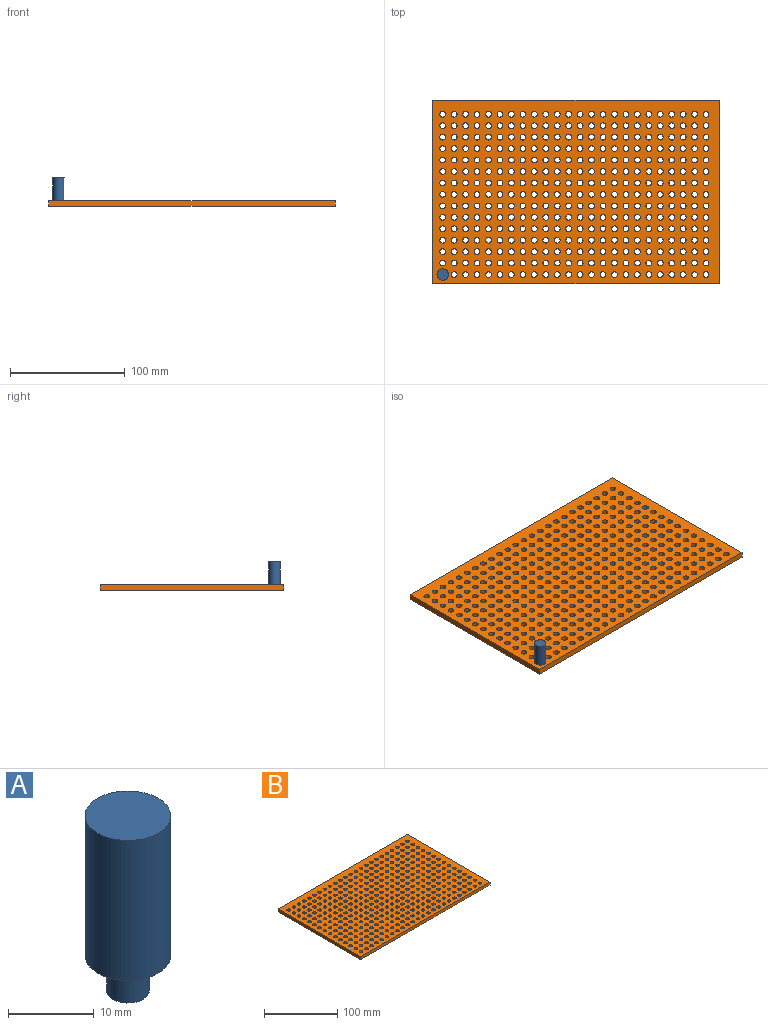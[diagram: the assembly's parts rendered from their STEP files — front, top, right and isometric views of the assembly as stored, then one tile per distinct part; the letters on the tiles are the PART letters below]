
ASSEMBLY  parts=2 mates=1
PART A: 5 faces, bbox 10x10x25 mm
  f0: plane 10x10mm, normal (0,0,-1), area 58.9mm2, adj f1,f4
  f1: cylinder r=2.5mm len=5mm, axis (0,0,-1), area 78.5mm2, adj f0,f2
  f2: plane 5x5mm, normal (0,0,-1), area 19.6mm2, adj f1
  f3: plane 10x10mm, normal (0,0,1), area 78.5mm2, adj f4
  f4: cylinder r=5mm len=20mm, axis (0,0,-1), area 628.3mm2, adj f0,f3
PART B: 366 faces, bbox 250x160x5 mm
  f0: plane 160x5mm, normal (1,0,0), area 800mm2, adj f1,f363,f364,f365
  f1: plane 250x5mm, normal (0,1,0), area 1250mm2, adj f0,f2,f364,f365
  f2: plane 160x5mm, normal (-1,0,0), area 800mm2, adj f1,f363,f364,f365
  f3: cylinder r=2.5mm len=5mm, axis (0,0,-1), area 78.5mm2, adj f364,f365
  f4: cylinder r=2.5mm len=5mm, axis (0,0,-1), area 78.5mm2, adj f364,f365
  f5: cylinder r=2.5mm len=5mm, axis (0,0,-1), area 78.5mm2, adj f364,f365
  f6: cylinder r=2.5mm len=5mm, axis (0,0,-1), area 78.5mm2, adj f364,f365
  f7: cylinder r=2.5mm len=5mm, axis (0,0,-1), area 78.5mm2, adj f364,f365
  f8: cylinder r=2.5mm len=5mm, axis (0,0,-1), area 78.5mm2, adj f364,f365
  f9: cylinder r=2.5mm len=5mm, axis (0,0,-1), area 78.5mm2, adj f364,f365
  f10: cylinder r=2.5mm len=5mm, axis (0,0,-1), area 78.5mm2, adj f364,f365
  f11: cylinder r=2.5mm len=5mm, axis (0,0,-1), area 78.5mm2, adj f364,f365
  f12: cylinder r=2.5mm len=5mm, axis (0,0,-1), area 78.5mm2, adj f364,f365
  f13: cylinder r=2.5mm len=5mm, axis (0,0,-1), area 78.5mm2, adj f364,f365
  f14: cylinder r=2.5mm len=5mm, axis (0,0,-1), area 78.5mm2, adj f364,f365
  f15: cylinder r=2.5mm len=5mm, axis (0,0,-1), area 78.5mm2, adj f364,f365
  f16: cylinder r=2.5mm len=5mm, axis (0,0,-1), area 78.5mm2, adj f364,f365
  f17: cylinder r=2.5mm len=5mm, axis (0,0,-1), area 78.5mm2, adj f364,f365
  f18: cylinder r=2.5mm len=5mm, axis (0,0,-1), area 78.5mm2, adj f364,f365
  f19: cylinder r=2.5mm len=5mm, axis (0,0,-1), area 78.5mm2, adj f364,f365
  f20: cylinder r=2.5mm len=5mm, axis (0,0,-1), area 78.5mm2, adj f364,f365
  f21: cylinder r=2.5mm len=5mm, axis (0,0,-1), area 78.5mm2, adj f364,f365
  f22: cylinder r=2.5mm len=5mm, axis (0,0,-1), area 78.5mm2, adj f364,f365
  f23: cylinder r=2.5mm len=5mm, axis (0,0,-1), area 78.5mm2, adj f364,f365
  f24: cylinder r=2.5mm len=5mm, axis (0,0,-1), area 78.5mm2, adj f364,f365
  f25: cylinder r=2.5mm len=5mm, axis (0,0,-1), area 78.5mm2, adj f364,f365
  f26: cylinder r=2.5mm len=5mm, axis (0,0,-1), area 78.5mm2, adj f364,f365
  f27: cylinder r=2.5mm len=5mm, axis (0,0,-1), area 78.5mm2, adj f364,f365
  f28: cylinder r=2.5mm len=5mm, axis (0,0,-1), area 78.5mm2, adj f364,f365
  f29: cylinder r=2.5mm len=5mm, axis (0,0,-1), area 78.5mm2, adj f364,f365
  f30: cylinder r=2.5mm len=5mm, axis (0,0,-1), area 78.5mm2, adj f364,f365
  f31: cylinder r=2.5mm len=5mm, axis (0,0,-1), area 78.5mm2, adj f364,f365
  f32: cylinder r=2.5mm len=5mm, axis (0,0,-1), area 78.5mm2, adj f364,f365
  f33: cylinder r=2.5mm len=5mm, axis (0,0,-1), area 78.5mm2, adj f364,f365
  f34: cylinder r=2.5mm len=5mm, axis (0,0,-1), area 78.5mm2, adj f364,f365
  f35: cylinder r=2.5mm len=5mm, axis (0,0,-1), area 78.5mm2, adj f364,f365
  f36: cylinder r=2.5mm len=5mm, axis (0,0,-1), area 78.5mm2, adj f364,f365
  f37: cylinder r=2.5mm len=5mm, axis (0,0,-1), area 78.5mm2, adj f364,f365
  f38: cylinder r=2.5mm len=5mm, axis (0,0,-1), area 78.5mm2, adj f364,f365
  f39: cylinder r=2.5mm len=5mm, axis (0,0,-1), area 78.5mm2, adj f364,f365
  f40: cylinder r=2.5mm len=5mm, axis (0,0,-1), area 78.5mm2, adj f364,f365
  f41: cylinder r=2.5mm len=5mm, axis (0,0,-1), area 78.5mm2, adj f364,f365
  f42: cylinder r=2.5mm len=5mm, axis (0,0,-1), area 78.5mm2, adj f364,f365
  f43: cylinder r=2.5mm len=5mm, axis (0,0,-1), area 78.5mm2, adj f364,f365
  f44: cylinder r=2.5mm len=5mm, axis (0,0,-1), area 78.5mm2, adj f364,f365
  f45: cylinder r=2.5mm len=5mm, axis (0,0,-1), area 78.5mm2, adj f364,f365
  f46: cylinder r=2.5mm len=5mm, axis (0,0,-1), area 78.5mm2, adj f364,f365
  f47: cylinder r=2.5mm len=5mm, axis (0,0,-1), area 78.5mm2, adj f364,f365
  f48: cylinder r=2.5mm len=5mm, axis (0,0,-1), area 78.5mm2, adj f364,f365
  f49: cylinder r=2.5mm len=5mm, axis (0,0,-1), area 78.5mm2, adj f364,f365
  f50: cylinder r=2.5mm len=5mm, axis (0,0,-1), area 78.5mm2, adj f364,f365
  f51: cylinder r=2.5mm len=5mm, axis (0,0,-1), area 78.5mm2, adj f364,f365
  f52: cylinder r=2.5mm len=5mm, axis (0,0,-1), area 78.5mm2, adj f364,f365
  f53: cylinder r=2.5mm len=5mm, axis (0,0,-1), area 78.5mm2, adj f364,f365
  f54: cylinder r=2.5mm len=5mm, axis (0,0,-1), area 78.5mm2, adj f364,f365
  f55: cylinder r=2.5mm len=5mm, axis (0,0,-1), area 78.5mm2, adj f364,f365
  f56: cylinder r=2.5mm len=5mm, axis (0,0,-1), area 78.5mm2, adj f364,f365
  f57: cylinder r=2.5mm len=5mm, axis (0,0,-1), area 78.5mm2, adj f364,f365
  f58: cylinder r=2.5mm len=5mm, axis (0,0,-1), area 78.5mm2, adj f364,f365
  f59: cylinder r=2.5mm len=5mm, axis (0,0,-1), area 78.5mm2, adj f364,f365
  f60: cylinder r=2.5mm len=5mm, axis (0,0,-1), area 78.5mm2, adj f364,f365
  f61: cylinder r=2.5mm len=5mm, axis (0,0,-1), area 78.5mm2, adj f364,f365
  f62: cylinder r=2.5mm len=5mm, axis (0,0,-1), area 78.5mm2, adj f364,f365
  f63: cylinder r=2.5mm len=5mm, axis (0,0,-1), area 78.5mm2, adj f364,f365
  f64: cylinder r=2.5mm len=5mm, axis (0,0,-1), area 78.5mm2, adj f364,f365
  f65: cylinder r=2.5mm len=5mm, axis (0,0,-1), area 78.5mm2, adj f364,f365
  f66: cylinder r=2.5mm len=5mm, axis (0,0,-1), area 78.5mm2, adj f364,f365
  f67: cylinder r=2.5mm len=5mm, axis (0,0,-1), area 78.5mm2, adj f364,f365
  f68: cylinder r=2.5mm len=5mm, axis (0,0,-1), area 78.5mm2, adj f364,f365
  f69: cylinder r=2.5mm len=5mm, axis (0,0,-1), area 78.5mm2, adj f364,f365
  f70: cylinder r=2.5mm len=5mm, axis (0,0,-1), area 78.5mm2, adj f364,f365
  f71: cylinder r=2.5mm len=5mm, axis (0,0,-1), area 78.5mm2, adj f364,f365
  f72: cylinder r=2.5mm len=5mm, axis (0,0,-1), area 78.5mm2, adj f364,f365
  f73: cylinder r=2.5mm len=5mm, axis (0,0,-1), area 78.5mm2, adj f364,f365
  f74: cylinder r=2.5mm len=5mm, axis (0,0,-1), area 78.5mm2, adj f364,f365
  f75: cylinder r=2.5mm len=5mm, axis (0,0,-1), area 78.5mm2, adj f364,f365
  f76: cylinder r=2.5mm len=5mm, axis (0,0,-1), area 78.5mm2, adj f364,f365
  f77: cylinder r=2.5mm len=5mm, axis (0,0,-1), area 78.5mm2, adj f364,f365
  f78: cylinder r=2.5mm len=5mm, axis (0,0,-1), area 78.5mm2, adj f364,f365
  f79: cylinder r=2.5mm len=5mm, axis (0,0,-1), area 78.5mm2, adj f364,f365
  f80: cylinder r=2.5mm len=5mm, axis (0,0,-1), area 78.5mm2, adj f364,f365
  f81: cylinder r=2.5mm len=5mm, axis (0,0,-1), area 78.5mm2, adj f364,f365
  f82: cylinder r=2.5mm len=5mm, axis (0,0,-1), area 78.5mm2, adj f364,f365
  f83: cylinder r=2.5mm len=5mm, axis (0,0,-1), area 78.5mm2, adj f364,f365
  f84: cylinder r=2.5mm len=5mm, axis (0,0,-1), area 78.5mm2, adj f364,f365
  f85: cylinder r=2.5mm len=5mm, axis (0,0,-1), area 78.5mm2, adj f364,f365
  f86: cylinder r=2.5mm len=5mm, axis (0,0,-1), area 78.5mm2, adj f364,f365
  f87: cylinder r=2.5mm len=5mm, axis (0,0,-1), area 78.5mm2, adj f364,f365
  f88: cylinder r=2.5mm len=5mm, axis (0,0,-1), area 78.5mm2, adj f364,f365
  f89: cylinder r=2.5mm len=5mm, axis (0,0,-1), area 78.5mm2, adj f364,f365
  f90: cylinder r=2.5mm len=5mm, axis (0,0,-1), area 78.5mm2, adj f364,f365
  f91: cylinder r=2.5mm len=5mm, axis (0,0,-1), area 78.5mm2, adj f364,f365
  f92: cylinder r=2.5mm len=5mm, axis (0,0,-1), area 78.5mm2, adj f364,f365
  f93: cylinder r=2.5mm len=5mm, axis (0,0,-1), area 78.5mm2, adj f364,f365
  f94: cylinder r=2.5mm len=5mm, axis (0,0,-1), area 78.5mm2, adj f364,f365
  f95: cylinder r=2.5mm len=5mm, axis (0,0,-1), area 78.5mm2, adj f364,f365
  f96: cylinder r=2.5mm len=5mm, axis (0,0,-1), area 78.5mm2, adj f364,f365
  f97: cylinder r=2.5mm len=5mm, axis (0,0,-1), area 78.5mm2, adj f364,f365
  f98: cylinder r=2.5mm len=5mm, axis (0,0,-1), area 78.5mm2, adj f364,f365
  f99: cylinder r=2.5mm len=5mm, axis (0,0,-1), area 78.5mm2, adj f364,f365
  f100: cylinder r=2.5mm len=5mm, axis (0,0,-1), area 78.5mm2, adj f364,f365
  f101: cylinder r=2.5mm len=5mm, axis (0,0,-1), area 78.5mm2, adj f364,f365
  f102: cylinder r=2.5mm len=5mm, axis (0,0,-1), area 78.5mm2, adj f364,f365
  f103: cylinder r=2.5mm len=5mm, axis (0,0,-1), area 78.5mm2, adj f364,f365
  f104: cylinder r=2.5mm len=5mm, axis (0,0,-1), area 78.5mm2, adj f364,f365
  f105: cylinder r=2.5mm len=5mm, axis (0,0,-1), area 78.5mm2, adj f364,f365
  f106: cylinder r=2.5mm len=5mm, axis (0,0,-1), area 78.5mm2, adj f364,f365
  f107: cylinder r=2.5mm len=5mm, axis (0,0,-1), area 78.5mm2, adj f364,f365
  f108: cylinder r=2.5mm len=5mm, axis (0,0,-1), area 78.5mm2, adj f364,f365
  f109: cylinder r=2.5mm len=5mm, axis (0,0,-1), area 78.5mm2, adj f364,f365
  f110: cylinder r=2.5mm len=5mm, axis (0,0,-1), area 78.5mm2, adj f364,f365
  f111: cylinder r=2.5mm len=5mm, axis (0,0,-1), area 78.5mm2, adj f364,f365
  f112: cylinder r=2.5mm len=5mm, axis (0,0,-1), area 78.5mm2, adj f364,f365
  f113: cylinder r=2.5mm len=5mm, axis (0,0,-1), area 78.5mm2, adj f364,f365
  f114: cylinder r=2.5mm len=5mm, axis (0,0,-1), area 78.5mm2, adj f364,f365
  f115: cylinder r=2.5mm len=5mm, axis (0,0,-1), area 78.5mm2, adj f364,f365
  f116: cylinder r=2.5mm len=5mm, axis (0,0,-1), area 78.5mm2, adj f364,f365
  f117: cylinder r=2.5mm len=5mm, axis (0,0,-1), area 78.5mm2, adj f364,f365
  f118: cylinder r=2.5mm len=5mm, axis (0,0,-1), area 78.5mm2, adj f364,f365
  f119: cylinder r=2.5mm len=5mm, axis (0,0,-1), area 78.5mm2, adj f364,f365
  f120: cylinder r=2.5mm len=5mm, axis (0,0,-1), area 78.5mm2, adj f364,f365
  f121: cylinder r=2.5mm len=5mm, axis (0,0,-1), area 78.5mm2, adj f364,f365
  f122: cylinder r=2.5mm len=5mm, axis (0,0,-1), area 78.5mm2, adj f364,f365
  f123: cylinder r=2.5mm len=5mm, axis (0,0,-1), area 78.5mm2, adj f364,f365
  f124: cylinder r=2.5mm len=5mm, axis (0,0,-1), area 78.5mm2, adj f364,f365
  f125: cylinder r=2.5mm len=5mm, axis (0,0,-1), area 78.5mm2, adj f364,f365
  f126: cylinder r=2.5mm len=5mm, axis (0,0,-1), area 78.5mm2, adj f364,f365
  f127: cylinder r=2.5mm len=5mm, axis (0,0,-1), area 78.5mm2, adj f364,f365
  f128: cylinder r=2.5mm len=5mm, axis (0,0,-1), area 78.5mm2, adj f364,f365
  f129: cylinder r=2.5mm len=5mm, axis (0,0,-1), area 78.5mm2, adj f364,f365
  f130: cylinder r=2.5mm len=5mm, axis (0,0,-1), area 78.5mm2, adj f364,f365
  f131: cylinder r=2.5mm len=5mm, axis (0,0,-1), area 78.5mm2, adj f364,f365
  f132: cylinder r=2.5mm len=5mm, axis (0,0,-1), area 78.5mm2, adj f364,f365
  f133: cylinder r=2.5mm len=5mm, axis (0,0,-1), area 78.5mm2, adj f364,f365
  f134: cylinder r=2.5mm len=5mm, axis (0,0,-1), area 78.5mm2, adj f364,f365
  f135: cylinder r=2.5mm len=5mm, axis (0,0,-1), area 78.5mm2, adj f364,f365
  f136: cylinder r=2.5mm len=5mm, axis (0,0,-1), area 78.5mm2, adj f364,f365
  f137: cylinder r=2.5mm len=5mm, axis (0,0,-1), area 78.5mm2, adj f364,f365
  f138: cylinder r=2.5mm len=5mm, axis (0,0,-1), area 78.5mm2, adj f364,f365
  f139: cylinder r=2.5mm len=5mm, axis (0,0,-1), area 78.5mm2, adj f364,f365
  f140: cylinder r=2.5mm len=5mm, axis (0,0,-1), area 78.5mm2, adj f364,f365
  f141: cylinder r=2.5mm len=5mm, axis (0,0,-1), area 78.5mm2, adj f364,f365
  f142: cylinder r=2.5mm len=5mm, axis (0,0,-1), area 78.5mm2, adj f364,f365
  f143: cylinder r=2.5mm len=5mm, axis (0,0,-1), area 78.5mm2, adj f364,f365
  f144: cylinder r=2.5mm len=5mm, axis (0,0,-1), area 78.5mm2, adj f364,f365
  f145: cylinder r=2.5mm len=5mm, axis (0,0,-1), area 78.5mm2, adj f364,f365
  f146: cylinder r=2.5mm len=5mm, axis (0,0,-1), area 78.5mm2, adj f364,f365
  f147: cylinder r=2.5mm len=5mm, axis (0,0,-1), area 78.5mm2, adj f364,f365
  f148: cylinder r=2.5mm len=5mm, axis (0,0,-1), area 78.5mm2, adj f364,f365
  f149: cylinder r=2.5mm len=5mm, axis (0,0,-1), area 78.5mm2, adj f364,f365
  f150: cylinder r=2.5mm len=5mm, axis (0,0,-1), area 78.5mm2, adj f364,f365
  f151: cylinder r=2.5mm len=5mm, axis (0,0,-1), area 78.5mm2, adj f364,f365
  f152: cylinder r=2.5mm len=5mm, axis (0,0,-1), area 78.5mm2, adj f364,f365
  f153: cylinder r=2.5mm len=5mm, axis (0,0,-1), area 78.5mm2, adj f364,f365
  f154: cylinder r=2.5mm len=5mm, axis (0,0,-1), area 78.5mm2, adj f364,f365
  f155: cylinder r=2.5mm len=5mm, axis (0,0,-1), area 78.5mm2, adj f364,f365
  f156: cylinder r=2.5mm len=5mm, axis (0,0,-1), area 78.5mm2, adj f364,f365
  f157: cylinder r=2.5mm len=5mm, axis (0,0,-1), area 78.5mm2, adj f364,f365
  f158: cylinder r=2.5mm len=5mm, axis (0,0,-1), area 78.5mm2, adj f364,f365
  f159: cylinder r=2.5mm len=5mm, axis (0,0,-1), area 78.5mm2, adj f364,f365
  f160: cylinder r=2.5mm len=5mm, axis (0,0,-1), area 78.5mm2, adj f364,f365
  f161: cylinder r=2.5mm len=5mm, axis (0,0,-1), area 78.5mm2, adj f364,f365
  f162: cylinder r=2.5mm len=5mm, axis (0,0,-1), area 78.5mm2, adj f364,f365
  f163: cylinder r=2.5mm len=5mm, axis (0,0,-1), area 78.5mm2, adj f364,f365
  f164: cylinder r=2.5mm len=5mm, axis (0,0,-1), area 78.5mm2, adj f364,f365
  f165: cylinder r=2.5mm len=5mm, axis (0,0,-1), area 78.5mm2, adj f364,f365
  f166: cylinder r=2.5mm len=5mm, axis (0,0,-1), area 78.5mm2, adj f364,f365
  f167: cylinder r=2.5mm len=5mm, axis (0,0,-1), area 78.5mm2, adj f364,f365
  f168: cylinder r=2.5mm len=5mm, axis (0,0,-1), area 78.5mm2, adj f364,f365
  f169: cylinder r=2.5mm len=5mm, axis (0,0,-1), area 78.5mm2, adj f364,f365
  f170: cylinder r=2.5mm len=5mm, axis (0,0,-1), area 78.5mm2, adj f364,f365
  f171: cylinder r=2.5mm len=5mm, axis (0,0,-1), area 78.5mm2, adj f364,f365
  f172: cylinder r=2.5mm len=5mm, axis (0,0,-1), area 78.5mm2, adj f364,f365
  f173: cylinder r=2.5mm len=5mm, axis (0,0,-1), area 78.5mm2, adj f364,f365
  f174: cylinder r=2.5mm len=5mm, axis (0,0,-1), area 78.5mm2, adj f364,f365
  f175: cylinder r=2.5mm len=5mm, axis (0,0,-1), area 78.5mm2, adj f364,f365
  f176: cylinder r=2.5mm len=5mm, axis (0,0,-1), area 78.5mm2, adj f364,f365
  f177: cylinder r=2.5mm len=5mm, axis (0,0,-1), area 78.5mm2, adj f364,f365
  f178: cylinder r=2.5mm len=5mm, axis (0,0,-1), area 78.5mm2, adj f364,f365
  f179: cylinder r=2.5mm len=5mm, axis (0,0,-1), area 78.5mm2, adj f364,f365
  f180: cylinder r=2.5mm len=5mm, axis (0,0,-1), area 78.5mm2, adj f364,f365
  f181: cylinder r=2.5mm len=5mm, axis (0,0,-1), area 78.5mm2, adj f364,f365
  f182: cylinder r=2.5mm len=5mm, axis (0,0,-1), area 78.5mm2, adj f364,f365
  f183: cylinder r=2.5mm len=5mm, axis (0,0,-1), area 78.5mm2, adj f364,f365
  f184: cylinder r=2.5mm len=5mm, axis (0,0,-1), area 78.5mm2, adj f364,f365
  f185: cylinder r=2.5mm len=5mm, axis (0,0,-1), area 78.5mm2, adj f364,f365
  f186: cylinder r=2.5mm len=5mm, axis (0,0,-1), area 78.5mm2, adj f364,f365
  f187: cylinder r=2.5mm len=5mm, axis (0,0,-1), area 78.5mm2, adj f364,f365
  f188: cylinder r=2.5mm len=5mm, axis (0,0,-1), area 78.5mm2, adj f364,f365
  f189: cylinder r=2.5mm len=5mm, axis (0,0,-1), area 78.5mm2, adj f364,f365
  f190: cylinder r=2.5mm len=5mm, axis (0,0,-1), area 78.5mm2, adj f364,f365
  f191: cylinder r=2.5mm len=5mm, axis (0,0,-1), area 78.5mm2, adj f364,f365
  f192: cylinder r=2.5mm len=5mm, axis (0,0,-1), area 78.5mm2, adj f364,f365
  f193: cylinder r=2.5mm len=5mm, axis (0,0,-1), area 78.5mm2, adj f364,f365
  f194: cylinder r=2.5mm len=5mm, axis (0,0,-1), area 78.5mm2, adj f364,f365
  f195: cylinder r=2.5mm len=5mm, axis (0,0,-1), area 78.5mm2, adj f364,f365
  f196: cylinder r=2.5mm len=5mm, axis (0,0,-1), area 78.5mm2, adj f364,f365
  f197: cylinder r=2.5mm len=5mm, axis (0,0,-1), area 78.5mm2, adj f364,f365
  f198: cylinder r=2.5mm len=5mm, axis (0,0,-1), area 78.5mm2, adj f364,f365
  f199: cylinder r=2.5mm len=5mm, axis (0,0,-1), area 78.5mm2, adj f364,f365
  f200: cylinder r=2.5mm len=5mm, axis (0,0,-1), area 78.5mm2, adj f364,f365
  f201: cylinder r=2.5mm len=5mm, axis (0,0,-1), area 78.5mm2, adj f364,f365
  f202: cylinder r=2.5mm len=5mm, axis (0,0,-1), area 78.5mm2, adj f364,f365
  f203: cylinder r=2.5mm len=5mm, axis (0,0,-1), area 78.5mm2, adj f364,f365
  f204: cylinder r=2.5mm len=5mm, axis (0,0,-1), area 78.5mm2, adj f364,f365
  f205: cylinder r=2.5mm len=5mm, axis (0,0,-1), area 78.5mm2, adj f364,f365
  f206: cylinder r=2.5mm len=5mm, axis (0,0,-1), area 78.5mm2, adj f364,f365
  f207: cylinder r=2.5mm len=5mm, axis (0,0,-1), area 78.5mm2, adj f364,f365
  f208: cylinder r=2.5mm len=5mm, axis (0,0,-1), area 78.5mm2, adj f364,f365
  f209: cylinder r=2.5mm len=5mm, axis (0,0,-1), area 78.5mm2, adj f364,f365
  f210: cylinder r=2.5mm len=5mm, axis (0,0,-1), area 78.5mm2, adj f364,f365
  f211: cylinder r=2.5mm len=5mm, axis (0,0,-1), area 78.5mm2, adj f364,f365
  f212: cylinder r=2.5mm len=5mm, axis (0,0,-1), area 78.5mm2, adj f364,f365
  f213: cylinder r=2.5mm len=5mm, axis (0,0,-1), area 78.5mm2, adj f364,f365
  f214: cylinder r=2.5mm len=5mm, axis (0,0,-1), area 78.5mm2, adj f364,f365
  f215: cylinder r=2.5mm len=5mm, axis (0,0,-1), area 78.5mm2, adj f364,f365
  f216: cylinder r=2.5mm len=5mm, axis (0,0,-1), area 78.5mm2, adj f364,f365
  f217: cylinder r=2.5mm len=5mm, axis (0,0,-1), area 78.5mm2, adj f364,f365
  f218: cylinder r=2.5mm len=5mm, axis (0,0,-1), area 78.5mm2, adj f364,f365
  f219: cylinder r=2.5mm len=5mm, axis (0,0,-1), area 78.5mm2, adj f364,f365
  f220: cylinder r=2.5mm len=5mm, axis (0,0,-1), area 78.5mm2, adj f364,f365
  f221: cylinder r=2.5mm len=5mm, axis (0,0,-1), area 78.5mm2, adj f364,f365
  f222: cylinder r=2.5mm len=5mm, axis (0,0,-1), area 78.5mm2, adj f364,f365
  f223: cylinder r=2.5mm len=5mm, axis (0,0,-1), area 78.5mm2, adj f364,f365
  f224: cylinder r=2.5mm len=5mm, axis (0,0,-1), area 78.5mm2, adj f364,f365
  f225: cylinder r=2.5mm len=5mm, axis (0,0,-1), area 78.5mm2, adj f364,f365
  f226: cylinder r=2.5mm len=5mm, axis (0,0,-1), area 78.5mm2, adj f364,f365
  f227: cylinder r=2.5mm len=5mm, axis (0,0,-1), area 78.5mm2, adj f364,f365
  f228: cylinder r=2.5mm len=5mm, axis (0,0,-1), area 78.5mm2, adj f364,f365
  f229: cylinder r=2.5mm len=5mm, axis (0,0,-1), area 78.5mm2, adj f364,f365
  f230: cylinder r=2.5mm len=5mm, axis (0,0,-1), area 78.5mm2, adj f364,f365
  f231: cylinder r=2.5mm len=5mm, axis (0,0,-1), area 78.5mm2, adj f364,f365
  f232: cylinder r=2.5mm len=5mm, axis (0,0,-1), area 78.5mm2, adj f364,f365
  f233: cylinder r=2.5mm len=5mm, axis (0,0,-1), area 78.5mm2, adj f364,f365
  f234: cylinder r=2.5mm len=5mm, axis (0,0,-1), area 78.5mm2, adj f364,f365
  f235: cylinder r=2.5mm len=5mm, axis (0,0,-1), area 78.5mm2, adj f364,f365
  f236: cylinder r=2.5mm len=5mm, axis (0,0,-1), area 78.5mm2, adj f364,f365
  f237: cylinder r=2.5mm len=5mm, axis (0,0,-1), area 78.5mm2, adj f364,f365
  f238: cylinder r=2.5mm len=5mm, axis (0,0,-1), area 78.5mm2, adj f364,f365
  f239: cylinder r=2.5mm len=5mm, axis (0,0,-1), area 78.5mm2, adj f364,f365
  f240: cylinder r=2.5mm len=5mm, axis (0,0,-1), area 78.5mm2, adj f364,f365
  f241: cylinder r=2.5mm len=5mm, axis (0,0,-1), area 78.5mm2, adj f364,f365
  f242: cylinder r=2.5mm len=5mm, axis (0,0,-1), area 78.5mm2, adj f364,f365
  f243: cylinder r=2.5mm len=5mm, axis (0,0,-1), area 78.5mm2, adj f364,f365
  f244: cylinder r=2.5mm len=5mm, axis (0,0,-1), area 78.5mm2, adj f364,f365
  f245: cylinder r=2.5mm len=5mm, axis (0,0,-1), area 78.5mm2, adj f364,f365
  f246: cylinder r=2.5mm len=5mm, axis (0,0,-1), area 78.5mm2, adj f364,f365
  f247: cylinder r=2.5mm len=5mm, axis (0,0,-1), area 78.5mm2, adj f364,f365
  f248: cylinder r=2.5mm len=5mm, axis (0,0,-1), area 78.5mm2, adj f364,f365
  f249: cylinder r=2.5mm len=5mm, axis (0,0,-1), area 78.5mm2, adj f364,f365
  f250: cylinder r=2.5mm len=5mm, axis (0,0,-1), area 78.5mm2, adj f364,f365
  f251: cylinder r=2.5mm len=5mm, axis (0,0,-1), area 78.5mm2, adj f364,f365
  f252: cylinder r=2.5mm len=5mm, axis (0,0,-1), area 78.5mm2, adj f364,f365
  f253: cylinder r=2.5mm len=5mm, axis (0,0,-1), area 78.5mm2, adj f364,f365
  f254: cylinder r=2.5mm len=5mm, axis (0,0,-1), area 78.5mm2, adj f364,f365
  f255: cylinder r=2.5mm len=5mm, axis (0,0,-1), area 78.5mm2, adj f364,f365
  f256: cylinder r=2.5mm len=5mm, axis (0,0,-1), area 78.5mm2, adj f364,f365
  f257: cylinder r=2.5mm len=5mm, axis (0,0,-1), area 78.5mm2, adj f364,f365
  f258: cylinder r=2.5mm len=5mm, axis (0,0,-1), area 78.5mm2, adj f364,f365
  f259: cylinder r=2.5mm len=5mm, axis (0,0,-1), area 78.5mm2, adj f364,f365
  f260: cylinder r=2.5mm len=5mm, axis (0,0,-1), area 78.5mm2, adj f364,f365
  f261: cylinder r=2.5mm len=5mm, axis (0,0,-1), area 78.5mm2, adj f364,f365
  f262: cylinder r=2.5mm len=5mm, axis (0,0,-1), area 78.5mm2, adj f364,f365
  f263: cylinder r=2.5mm len=5mm, axis (0,0,-1), area 78.5mm2, adj f364,f365
  f264: cylinder r=2.5mm len=5mm, axis (0,0,-1), area 78.5mm2, adj f364,f365
  f265: cylinder r=2.5mm len=5mm, axis (0,0,-1), area 78.5mm2, adj f364,f365
  f266: cylinder r=2.5mm len=5mm, axis (0,0,-1), area 78.5mm2, adj f364,f365
  f267: cylinder r=2.5mm len=5mm, axis (0,0,-1), area 78.5mm2, adj f364,f365
  f268: cylinder r=2.5mm len=5mm, axis (0,0,-1), area 78.5mm2, adj f364,f365
  f269: cylinder r=2.5mm len=5mm, axis (0,0,-1), area 78.5mm2, adj f364,f365
  f270: cylinder r=2.5mm len=5mm, axis (0,0,-1), area 78.5mm2, adj f364,f365
  f271: cylinder r=2.5mm len=5mm, axis (0,0,-1), area 78.5mm2, adj f364,f365
  f272: cylinder r=2.5mm len=5mm, axis (0,0,-1), area 78.5mm2, adj f364,f365
  f273: cylinder r=2.5mm len=5mm, axis (0,0,-1), area 78.5mm2, adj f364,f365
  f274: cylinder r=2.5mm len=5mm, axis (0,0,-1), area 78.5mm2, adj f364,f365
  f275: cylinder r=2.5mm len=5mm, axis (0,0,-1), area 78.5mm2, adj f364,f365
  f276: cylinder r=2.5mm len=5mm, axis (0,0,-1), area 78.5mm2, adj f364,f365
  f277: cylinder r=2.5mm len=5mm, axis (0,0,-1), area 78.5mm2, adj f364,f365
  f278: cylinder r=2.5mm len=5mm, axis (0,0,-1), area 78.5mm2, adj f364,f365
  f279: cylinder r=2.5mm len=5mm, axis (0,0,-1), area 78.5mm2, adj f364,f365
  f280: cylinder r=2.5mm len=5mm, axis (0,0,-1), area 78.5mm2, adj f364,f365
  f281: cylinder r=2.5mm len=5mm, axis (0,0,-1), area 78.5mm2, adj f364,f365
  f282: cylinder r=2.5mm len=5mm, axis (0,0,-1), area 78.5mm2, adj f364,f365
  f283: cylinder r=2.5mm len=5mm, axis (0,0,-1), area 78.5mm2, adj f364,f365
  f284: cylinder r=2.5mm len=5mm, axis (0,0,-1), area 78.5mm2, adj f364,f365
  f285: cylinder r=2.5mm len=5mm, axis (0,0,-1), area 78.5mm2, adj f364,f365
  f286: cylinder r=2.5mm len=5mm, axis (0,0,-1), area 78.5mm2, adj f364,f365
  f287: cylinder r=2.5mm len=5mm, axis (0,0,-1), area 78.5mm2, adj f364,f365
  f288: cylinder r=2.5mm len=5mm, axis (0,0,-1), area 78.5mm2, adj f364,f365
  f289: cylinder r=2.5mm len=5mm, axis (0,0,-1), area 78.5mm2, adj f364,f365
  f290: cylinder r=2.5mm len=5mm, axis (0,0,-1), area 78.5mm2, adj f364,f365
  f291: cylinder r=2.5mm len=5mm, axis (0,0,-1), area 78.5mm2, adj f364,f365
  f292: cylinder r=2.5mm len=5mm, axis (0,0,-1), area 78.5mm2, adj f364,f365
  f293: cylinder r=2.5mm len=5mm, axis (0,0,-1), area 78.5mm2, adj f364,f365
  f294: cylinder r=2.5mm len=5mm, axis (0,0,-1), area 78.5mm2, adj f364,f365
  f295: cylinder r=2.5mm len=5mm, axis (0,0,-1), area 78.5mm2, adj f364,f365
  f296: cylinder r=2.5mm len=5mm, axis (0,0,-1), area 78.5mm2, adj f364,f365
  f297: cylinder r=2.5mm len=5mm, axis (0,0,-1), area 78.5mm2, adj f364,f365
  f298: cylinder r=2.5mm len=5mm, axis (0,0,-1), area 78.5mm2, adj f364,f365
  f299: cylinder r=2.5mm len=5mm, axis (0,0,-1), area 78.5mm2, adj f364,f365
  f300: cylinder r=2.5mm len=5mm, axis (0,0,-1), area 78.5mm2, adj f364,f365
  f301: cylinder r=2.5mm len=5mm, axis (0,0,-1), area 78.5mm2, adj f364,f365
  f302: cylinder r=2.5mm len=5mm, axis (0,0,-1), area 78.5mm2, adj f364,f365
  f303: cylinder r=2.5mm len=5mm, axis (0,0,-1), area 78.5mm2, adj f364,f365
  f304: cylinder r=2.5mm len=5mm, axis (0,0,-1), area 78.5mm2, adj f364,f365
  f305: cylinder r=2.5mm len=5mm, axis (0,0,-1), area 78.5mm2, adj f364,f365
  f306: cylinder r=2.5mm len=5mm, axis (0,0,-1), area 78.5mm2, adj f364,f365
  f307: cylinder r=2.5mm len=5mm, axis (0,0,-1), area 78.5mm2, adj f364,f365
  f308: cylinder r=2.5mm len=5mm, axis (0,0,-1), area 78.5mm2, adj f364,f365
  f309: cylinder r=2.5mm len=5mm, axis (0,0,-1), area 78.5mm2, adj f364,f365
  f310: cylinder r=2.5mm len=5mm, axis (0,0,-1), area 78.5mm2, adj f364,f365
  f311: cylinder r=2.5mm len=5mm, axis (0,0,-1), area 78.5mm2, adj f364,f365
  f312: cylinder r=2.5mm len=5mm, axis (0,0,-1), area 78.5mm2, adj f364,f365
  f313: cylinder r=2.5mm len=5mm, axis (0,0,-1), area 78.5mm2, adj f364,f365
  f314: cylinder r=2.5mm len=5mm, axis (0,0,-1), area 78.5mm2, adj f364,f365
  f315: cylinder r=2.5mm len=5mm, axis (0,0,-1), area 78.5mm2, adj f364,f365
  f316: cylinder r=2.5mm len=5mm, axis (0,0,-1), area 78.5mm2, adj f364,f365
  f317: cylinder r=2.5mm len=5mm, axis (0,0,-1), area 78.5mm2, adj f364,f365
  f318: cylinder r=2.5mm len=5mm, axis (0,0,-1), area 78.5mm2, adj f364,f365
  f319: cylinder r=2.5mm len=5mm, axis (0,0,-1), area 78.5mm2, adj f364,f365
  f320: cylinder r=2.5mm len=5mm, axis (0,0,-1), area 78.5mm2, adj f364,f365
  f321: cylinder r=2.5mm len=5mm, axis (0,0,-1), area 78.5mm2, adj f364,f365
  f322: cylinder r=2.5mm len=5mm, axis (0,0,-1), area 78.5mm2, adj f364,f365
  f323: cylinder r=2.5mm len=5mm, axis (0,0,-1), area 78.5mm2, adj f364,f365
  f324: cylinder r=2.5mm len=5mm, axis (0,0,-1), area 78.5mm2, adj f364,f365
  f325: cylinder r=2.5mm len=5mm, axis (0,0,-1), area 78.5mm2, adj f364,f365
  f326: cylinder r=2.5mm len=5mm, axis (0,0,-1), area 78.5mm2, adj f364,f365
  f327: cylinder r=2.5mm len=5mm, axis (0,0,-1), area 78.5mm2, adj f364,f365
  f328: cylinder r=2.5mm len=5mm, axis (0,0,-1), area 78.5mm2, adj f364,f365
  f329: cylinder r=2.5mm len=5mm, axis (0,0,-1), area 78.5mm2, adj f364,f365
  f330: cylinder r=2.5mm len=5mm, axis (0,0,-1), area 78.5mm2, adj f364,f365
  f331: cylinder r=2.5mm len=5mm, axis (0,0,-1), area 78.5mm2, adj f364,f365
  f332: cylinder r=2.5mm len=5mm, axis (0,0,-1), area 78.5mm2, adj f364,f365
  f333: cylinder r=2.5mm len=5mm, axis (0,0,-1), area 78.5mm2, adj f364,f365
  f334: cylinder r=2.5mm len=5mm, axis (0,0,-1), area 78.5mm2, adj f364,f365
  f335: cylinder r=2.5mm len=5mm, axis (0,0,-1), area 78.5mm2, adj f364,f365
  f336: cylinder r=2.5mm len=5mm, axis (0,0,-1), area 78.5mm2, adj f364,f365
  f337: cylinder r=2.5mm len=5mm, axis (0,0,-1), area 78.5mm2, adj f364,f365
  f338: cylinder r=2.5mm len=5mm, axis (0,0,-1), area 78.5mm2, adj f364,f365
  f339: cylinder r=2.5mm len=5mm, axis (0,0,-1), area 78.5mm2, adj f364,f365
  f340: cylinder r=2.5mm len=5mm, axis (0,0,-1), area 78.5mm2, adj f364,f365
  f341: cylinder r=2.5mm len=5mm, axis (0,0,-1), area 78.5mm2, adj f364,f365
  f342: cylinder r=2.5mm len=5mm, axis (0,0,-1), area 78.5mm2, adj f364,f365
  f343: cylinder r=2.5mm len=5mm, axis (0,0,-1), area 78.5mm2, adj f364,f365
  f344: cylinder r=2.5mm len=5mm, axis (0,0,-1), area 78.5mm2, adj f364,f365
  f345: cylinder r=2.5mm len=5mm, axis (0,0,-1), area 78.5mm2, adj f364,f365
  f346: cylinder r=2.5mm len=5mm, axis (0,0,-1), area 78.5mm2, adj f364,f365
  f347: cylinder r=2.5mm len=5mm, axis (0,0,-1), area 78.5mm2, adj f364,f365
  f348: cylinder r=2.5mm len=5mm, axis (0,0,-1), area 78.5mm2, adj f364,f365
  f349: cylinder r=2.5mm len=5mm, axis (0,0,-1), area 78.5mm2, adj f364,f365
  f350: cylinder r=2.5mm len=5mm, axis (0,0,-1), area 78.5mm2, adj f364,f365
  f351: cylinder r=2.5mm len=5mm, axis (0,0,-1), area 78.5mm2, adj f364,f365
  f352: cylinder r=2.5mm len=5mm, axis (0,0,-1), area 78.5mm2, adj f364,f365
  f353: cylinder r=2.5mm len=5mm, axis (0,0,-1), area 78.5mm2, adj f364,f365
  f354: cylinder r=2.5mm len=5mm, axis (0,0,-1), area 78.5mm2, adj f364,f365
  f355: cylinder r=2.5mm len=5mm, axis (0,0,-1), area 78.5mm2, adj f364,f365
  f356: cylinder r=2.5mm len=5mm, axis (0,0,-1), area 78.5mm2, adj f364,f365
  f357: cylinder r=2.5mm len=5mm, axis (0,0,-1), area 78.5mm2, adj f364,f365
  f358: cylinder r=2.5mm len=5mm, axis (0,0,-1), area 78.5mm2, adj f364,f365
  f359: cylinder r=2.5mm len=5mm, axis (0,0,-1), area 78.5mm2, adj f364,f365
  f360: cylinder r=2.5mm len=5mm, axis (0,0,-1), area 78.5mm2, adj f364,f365
  f361: cylinder r=2.5mm len=5mm, axis (0,0,-1), area 78.5mm2, adj f364,f365
  f362: cylinder r=2.5mm len=5mm, axis (0,0,-1), area 78.5mm2, adj f364,f365
  f363: plane 250x5mm, normal (0,-1,0), area 1250mm2, adj f0,f2,f364,f365
  f364: plane 250x160mm, normal (0,0,1), area 32931.4mm2, adj f0,f1,f2,f3,f4,f5,f6,f7
  f365: plane 250x160mm, normal (0,0,-1), area 32931.4mm2, adj f0,f1,f2,f3,f4,f5,f6,f7
PLACE A t=(-119.16,-93.08,-33.93)mm
PLACE B t=(-2.78,-20.96,-33.93)mm
MATE fastened A.f1 <-> B.f3  axis (0,0,-1) through (-119.16,-93.08,-28.93)mm
